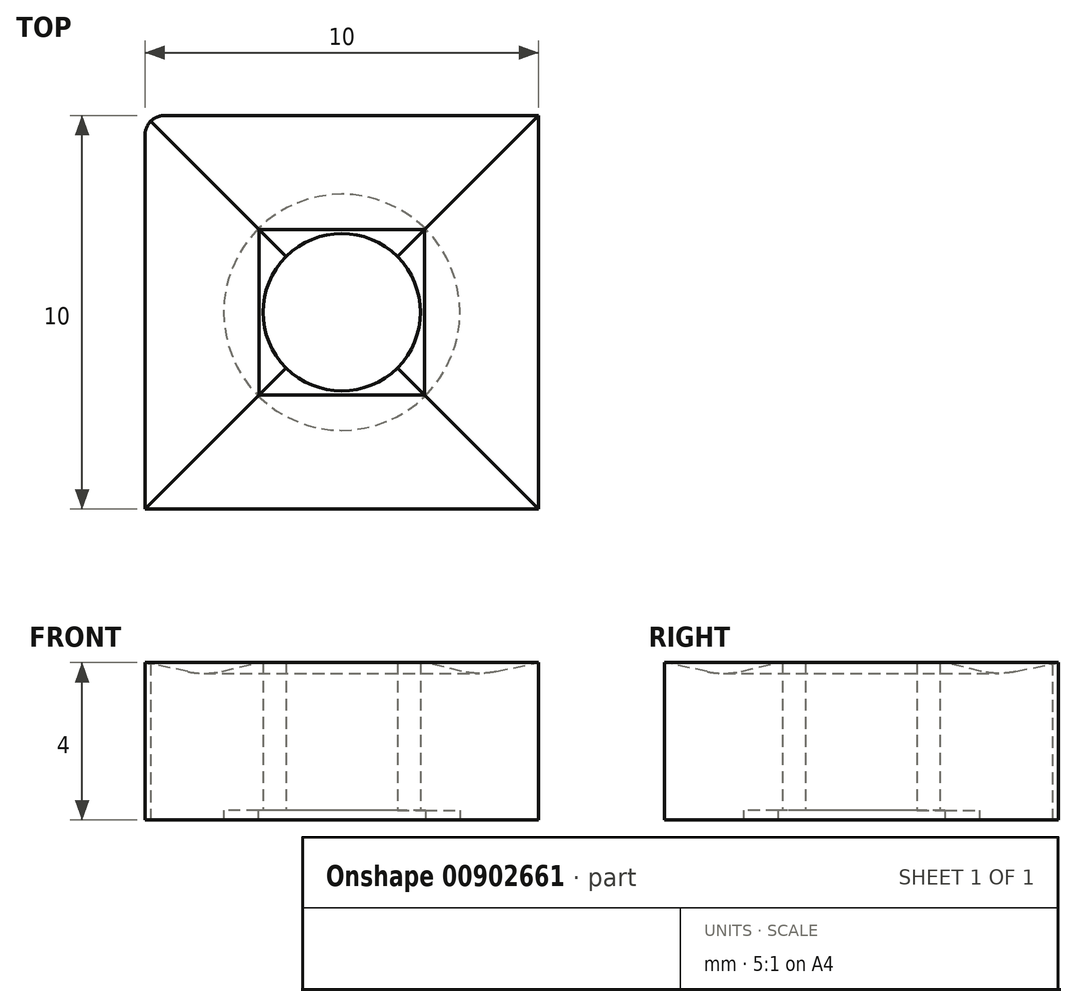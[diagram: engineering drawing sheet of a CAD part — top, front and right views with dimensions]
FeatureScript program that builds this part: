
annotation { "Feature Type Name" : "Feature", "Feature Type Description" : "" }
export const myFeature = defineFeature(function(context is Context, id is Id, definition is map)
    precondition{}
    {
        {
            var Q0;
            Q0=qCreatedBy(makeId("Right.planeOp"),FACE);
            var sketch = newSketch(context, id + "F0", { "sketchPlane" : qUnion([Q0])});
            skLineSegment(sketch, "E0.bottom", {"start": v(0, 0) * mm, "end": v(5, 0) * mm});
            skLineSegment(sketch, "E0.top", {"start": v(0, 4) * mm, "end": v(2.1, 4) * mm});
            skLineSegment(sketch, "E0.left", {"start": v(0, 0) * mm, "end": v(0, 4) * mm});
            skLineSegment(sketch, "E0.right", {"start": v(5, 0) * mm, "end": v(5, 4) * mm});
            skLineSegment(sketch, "E1", {"start": v(0, 0) * mm, "end": v(0, 19.97) * mm, "construction": true});
            skLineSegment(sketch, "E2", {"start": v(2, 0) * mm, "end": v(2, 8.57) * mm, "construction": true});
            skArc(sketch, "E3", {"start": v(3.04, 3.78) * mm, "mid": v(3.48, 3.73) * mm, "end": v(3.92, 3.77) * mm});
            skLineSegment(sketch, "E4", {"start": v(5, 4) * mm, "end": v(3.92, 3.77) * mm});
            skLineSegment(sketch, "E5", {"start": v(2.1, 4) * mm, "end": v(3.04, 3.78) * mm});
            skLineSegment(sketch, "E6", {"start": v(5, 4) * mm, "end": v(2.1, 4) * mm, "construction": true});
            skSolve(sketch);
        }
        {
            var Q0;
            Q0=makeQuery(id+"F0.imprint","IMPRINT",FACE,{"disambiguationData":[TD([[makeQuery(id+"F0.imprint","IMPRINT",EDGE,{"derivedFrom":sQuery(id+"F0.wireOp",EDGE,"E0.bottom")}),1.0]])]});
            extrude(context, id + "F1", {"entities" : qUnion([Q0]), "endBound" : BoundingType.SYMMETRIC, "depth" : 10 * mm, "offsetDistance" : 25 * mm});
        }
        {
            var Q0;
            Q0=qCreatedBy(makeId("Top.planeOp"),FACE);
            var sketch = newSketch(context, id + "F2", { "sketchPlane" : qUnion([Q0])});
            skLineSegment(sketch, "E7", {"start": v(0, 0) * mm, "end": v(-6.08, 6.08) * mm});
            skLineSegment(sketch, "E8", {"start": v(-6.08, 6.08) * mm, "end": v(-6.22, 0) * mm});
            skLineSegment(sketch, "E9", {"start": v(0, 0) * mm, "end": v(0, 6.95) * mm, "construction": true});
            skLineSegment(sketch, "E10", {"start": v(0, 0) * mm, "end": v(6.22, 6.22) * mm});
            skLineSegment(sketch, "E11", {"start": v(6.22, 6.22) * mm, "end": v(5.35, -3.39) * mm});
            skLineSegment(sketch, "E12", {"start": v(5.35, -3.39) * mm, "end": v(-6.08, -3.13) * mm});
            skLineSegment(sketch, "E13", {"start": v(-6.08, -3.13) * mm, "end": v(-6.22, 0) * mm});
            skSolve(sketch);
        }
        {
            var Q0;
            Q0 = qSketchRegion(id + "F2", true);
            extrude(context, id + "F3", {"entities" : qUnion([Q0]), "operationType" : NewBodyOperationType.REMOVE, "endBound" : BoundingType.THROUGH_ALL, "depth" : 25 * mm, "offsetDistance" : 25 * mm});
        }
        {
            var Q0;
            Q0=makeQuery(id+"F1.opExtrude","SWEPT_BODY",BODY,{"disambiguationData":[OSD([sQuery(id+"F0.wireOp",EDGE,"E0.bottom"),sQuery(id+"F0.wireOp",EDGE,"E0.top"),sQuery(id+"F0.wireOp",EDGE,"E0.left"),sQuery(id+"F0.wireOp",EDGE,"E0.right"),sQuery(id+"F0.wireOp",EDGE,"E3"),sQuery(id+"F0.wireOp",EDGE,"E4"),sQuery(id+"F0.wireOp",EDGE,"E5")])]});
            var Q1;
            Q1=makeQuery(id+"F3.boolean.opBoolean","COPY",EDGE,{"derivedFrom":makeQuery(id+"F3.opExtrude","SWEPT_EDGE",EDGE,{"disambiguationData":[OSD([sQuery(id+"F2.wireOp",EDGE,"E7"),sQuery(id+"F2.wireOp",EDGE,"E10")])]})});
            circularPattern(context, id + "F4", {"entities" : qUnion([Q0]), "axis" : qUnion([Q1]), "angle" : 360 * degree, "instanceCount" : 4, "equalSpace" : true, "isCentered" : true});
        }
        {
            var Q0;
            Q0=qCreatedBy(makeId("Front.planeOp"),FACE);
            var sketch = newSketch(context, id + "F5", { "sketchPlane" : qUnion([Q0])});
            skLineSegment(sketch, "E14", {"start": v(-3, 0) * mm, "end": v(-3, 0.25) * mm});
            skLineSegment(sketch, "E15", {"start": v(-3, 0.25) * mm, "end": v(-2, 0.25) * mm});
            skLineSegment(sketch, "E16", {"start": v(-2, 0.25) * mm, "end": v(-2, 5.5) * mm});
            skLineSegment(sketch, "E17", {"start": v(-2, 5.5) * mm, "end": v(0, 5.5) * mm});
            skLineSegment(sketch, "E18", {"start": v(0, 5.5) * mm, "end": v(0, 0) * mm});
            skLineSegment(sketch, "E19", {"start": v(0, 0) * mm, "end": v(-3, 0) * mm});
            skSolve(sketch);
        }
        {
            var Q0;
            Q0 = qSketchRegion(id + "F5", true);
            var Q1;
            Q1=sQuery(id+"F5.wireOp",EDGE,"E18");
            revolve(context, id + "F6", {"operationType" : NewBodyOperationType.REMOVE, "surfaceOperationType" : NewSurfaceOperationType.NEW, "entities" : qUnion([Q0]), "axis" : qUnion([Q1]), "revolveType" : RevolveType.FULL, "oppositeDirection" : true});
        }
        {
            var Q0;
            Q0=qCreatedBy(makeId("Top.planeOp"),FACE);
            var sketch = newSketch(context, id + "F7", { "sketchPlane" : qUnion([Q0])});
            skArc(sketch, "E20", {"start": v(-4.5, 5) * mm, "mid": v(-4.85, 4.85) * mm, "end": v(-5, 4.5) * mm});
            skLineSegment(sketch, "E21", {"start": v(-5, 4.5) * mm, "end": v(-5.92, 4.5) * mm});
            skLineSegment(sketch, "E22", {"start": v(-5.92, 4.5) * mm, "end": v(-5.84, 6.2) * mm});
            skLineSegment(sketch, "E23", {"start": v(-5.84, 6.2) * mm, "end": v(-4.5, 6.27) * mm});
            skLineSegment(sketch, "E24", {"start": v(-4.5, 6.27) * mm, "end": v(-4.5, 5) * mm});
            skSolve(sketch);
        }
        {
            var Q0;
            Q0 = qSketchRegion(id + "F7", true);
            extrude(context, id + "F8", {"entities" : qUnion([Q0]), "operationType" : NewBodyOperationType.REMOVE, "depth" : 25 * mm, "offsetDistance" : 25 * mm});
        }
    });
